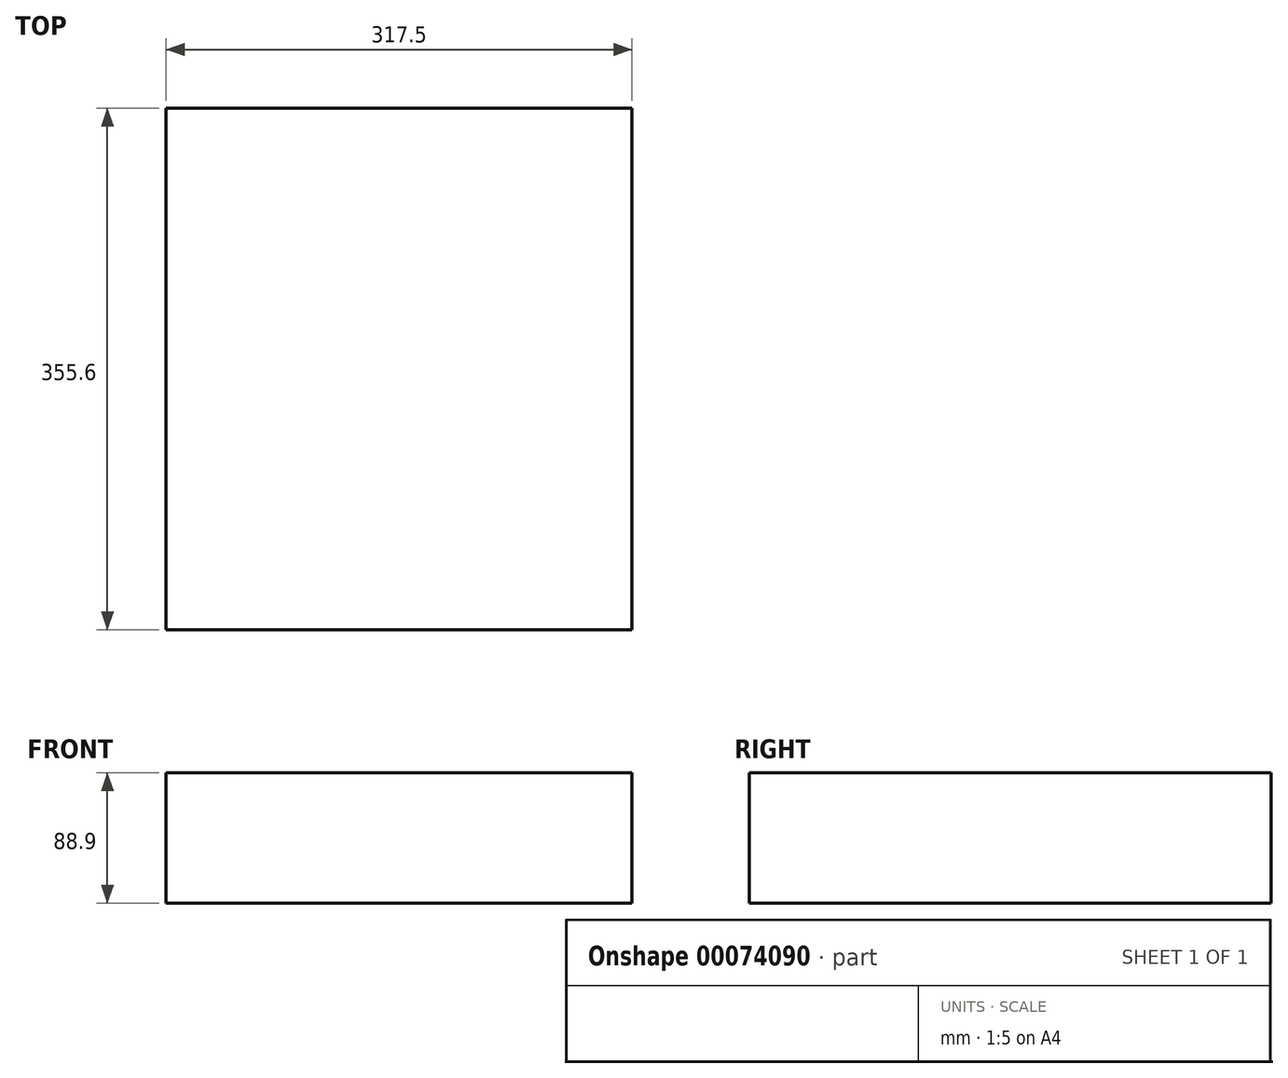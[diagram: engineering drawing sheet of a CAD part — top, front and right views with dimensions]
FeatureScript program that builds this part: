
annotation { "Feature Type Name" : "Feature", "Feature Type Description" : "" }
export const myFeature = defineFeature(function(context is Context, id is Id, definition is map)
    precondition{}
    {
        {
            var Q0;
            Q0=qCreatedBy(makeId("Top.planeOp"),FACE);
            var sketch = newSketch(context, id + "F0", { "sketchPlane" : qUnion([Q0])});
            skLineSegment(sketch, "E0.rect.bottom", {"start": v(158.75, -177.8) * mm, "end": v(-158.75, -177.8) * mm});
            skLineSegment(sketch, "E0.rect.top", {"start": v(158.75, 177.8) * mm, "end": v(-158.75, 177.8) * mm});
            skLineSegment(sketch, "E0.rect.left", {"start": v(158.75, -177.8) * mm, "end": v(158.75, 177.8) * mm});
            skLineSegment(sketch, "E0.rect.right", {"start": v(-158.75, -177.8) * mm, "end": v(-158.75, 177.8) * mm});
            skPoint(sketch, "E0.rect.middle", {"position": v(0, 0) * mm});
            skSolve(sketch);
        }
        {
            var Q0;
            Q0=makeQuery(id+"F0.imprint","IMPRINT",FACE,{"disambiguationData":[TD([[makeQuery(id+"F0.imprint","IMPRINT",EDGE,{"derivedFrom":sQuery(id+"F0.wireOp",EDGE,"E0.rect.bottom")}),-1.0]])]});
            extrude(context, id + "F1", {"entities" : qUnion([Q0]), "depth" : 88.9 * mm});
        }
    });
